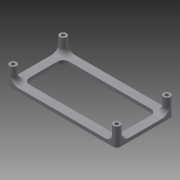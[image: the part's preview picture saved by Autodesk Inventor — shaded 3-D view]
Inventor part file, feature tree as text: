
AUTODESK INVENTOR PART (.ipt)
format: ipt  version: 2013 (Build 170138000, 138)  size: 192,512 bytes
history: native  units: mm
features: sketch x5, extrude x4, fillet x2, hole x1, projected_geometry x1
ambient origin geometry x8: Origin, YZ Plane, XZ Plane, XY Plane, X Axis, Y Axis, Z Axis, Center Point
bodies: Solid1 (feature_tree)
feature tree (13):
  extrude  "Extrusion1"  Depth=101.6mm
  hole  "Hole1"  [1 undecoded]
  extrude  "Extrusion2"  Depth=6.0mm
  extrude  "Extrusion3"  Depth=3.0mm TaperAngle=0.0deg
  extrude  "Extrusion4"  Depth=7.5mm
  fillet  "Fillet1"  Radius=7.5mm
  fillet  "Fillet2"  Radius=3.0mm
  sketch  "Sketch1"  dims[d0=50.8mm d2=101.6mm]
  sketch  "Sketch2"  dims[d3=16.0mm d4=0.0mm d5=43.815mm]
  sketch  "Sketch3"  dims[d7=90.678mm]
  sketch  "Sketch4"  dims[d8=3.0mm d9=6.0mm d10=6.5mm d11=3.0mm d12=90.0deg d13=8.0mm d14=20.594885mm d15=6.0mm]
  sketch  "Sketch5"  dims[d17=10.0mm d18=0.0mm d19=3.0mm d20=0.0mm d21=7.5mm d22=7.5mm d23=3.0mm d24=0.0mm d25=5.0mm d26=5.0mm]
  projected_geometry  "Project Cut Edges1"
note: 1 required parameter value undecoded (feature->parameter linkage not recoverable at this tier; creation-order binding heuristic only, values carry confidence <= 0.55)
